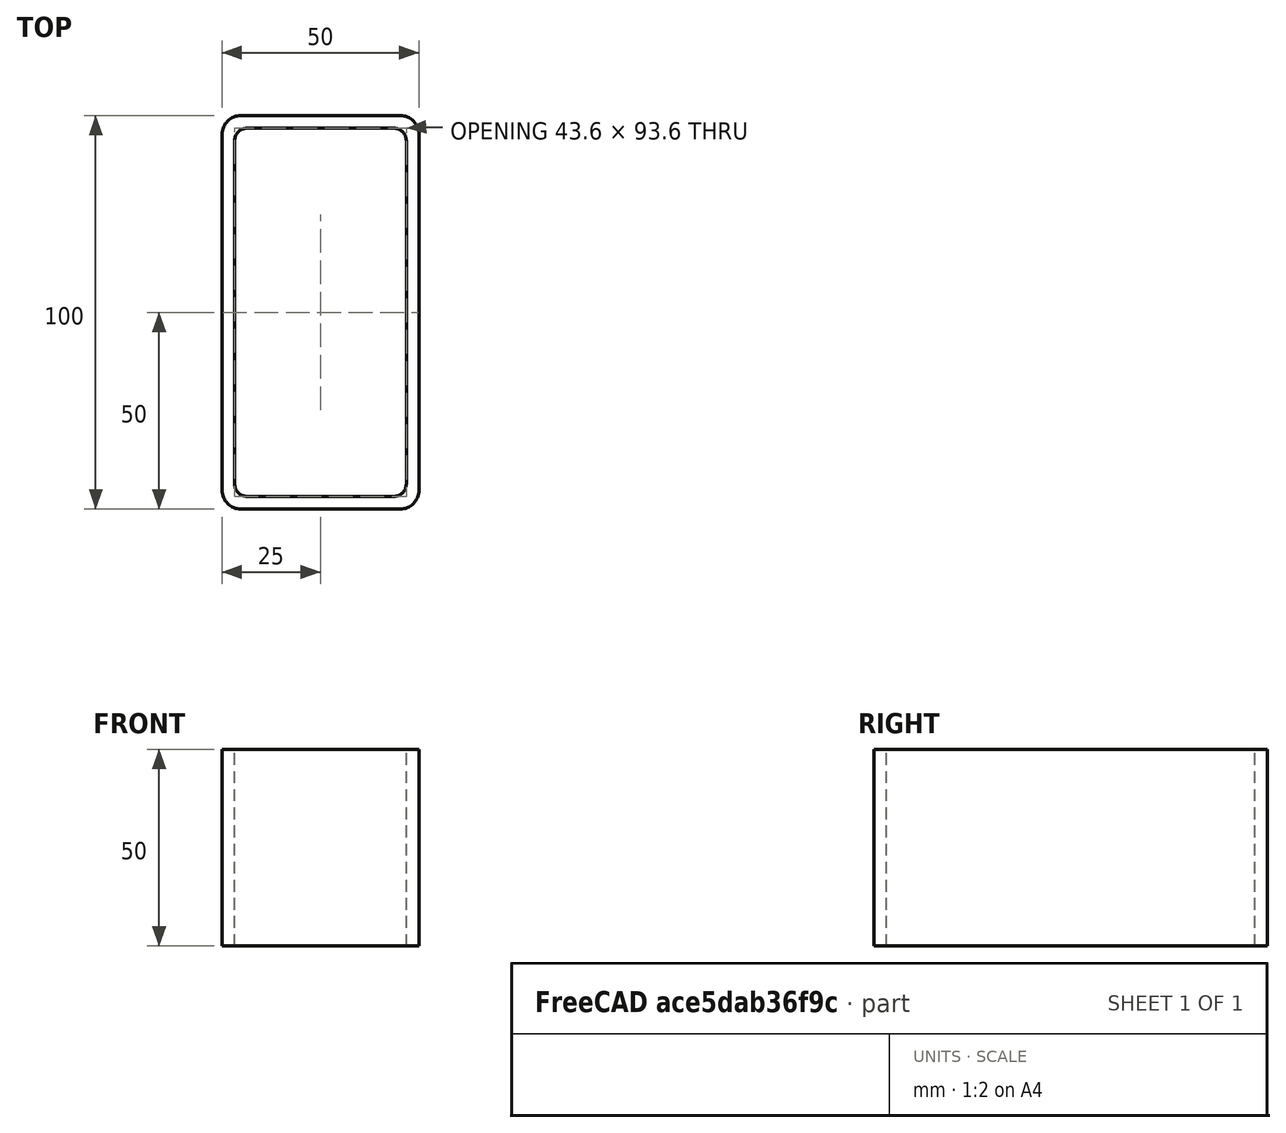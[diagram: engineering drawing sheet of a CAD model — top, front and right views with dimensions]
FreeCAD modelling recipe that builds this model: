
FCSTD DOCUMENT  (FreeCAD 0.15R4671 (Git))
Label: Rectangular hollow section 100x50x3.2 EN10219 S235JRH
License: All rights reserved
LicenseURL: http://en.wikipedia.org/wiki/All_rights_reserved
objects: Sketcher::SketchObject×1, Part::Extrusion×1
note: 2 computed .brp shape members not serialized (recipe doc carries the construction recipe); baked Part::Feature solids carry a one-line shape summary decoded from their .brp

FEATURE [Sketcher::SketchObject] Sketch
  sketch-geometry (16):
    g0: LineSegment StartX=-18.6 StartY=46.8 StartZ=0 EndX=18.6 EndY=46.8 EndZ=0
    g1: LineSegment StartX=21.8 StartY=43.6 StartZ=0 EndX=21.8 EndY=-43.6 EndZ=0
    g2: LineSegment StartX=18.6 StartY=-46.8 StartZ=0 EndX=-18.6 EndY=-46.8 EndZ=0
    g3: LineSegment StartX=-21.8 StartY=-43.6 StartZ=0 EndX=-21.8 EndY=43.6 EndZ=0
    g4: LineSegment StartX=-20.2 StartY=50 StartZ=0 EndX=20.2 EndY=50 EndZ=0
    g5: LineSegment StartX=25 StartY=45.2 StartZ=0 EndX=25 EndY=-45.2 EndZ=0
    g6: LineSegment StartX=20.2 StartY=-50 StartZ=0 EndX=-20.2 EndY=-50 EndZ=0
    g7: LineSegment StartX=-25 StartY=-45.2 StartZ=0 EndX=-25 EndY=45.2 EndZ=0
    g8: ArcOfCircle CenterX=-18.6 CenterY=43.6 CenterZ=0 NormalX=0 NormalY=0 NormalZ=1 Radius=3.2 StartAngle=1.5708 EndAngle=3.14159
    g9: ArcOfCircle CenterX=18.6 CenterY=43.6 CenterZ=0 NormalX=0 NormalY=0 NormalZ=1 Radius=3.2 StartAngle=0 EndAngle=1.5708
    g10: ArcOfCircle CenterX=18.6 CenterY=-43.6 CenterZ=0 NormalX=0 NormalY=0 NormalZ=1 Radius=3.2 StartAngle=4.71239 EndAngle=6.28319
    g11: ArcOfCircle CenterX=-18.6 CenterY=-43.6 CenterZ=0 NormalX=0 NormalY=0 NormalZ=1 Radius=3.2 StartAngle=3.14159 EndAngle=4.71239
    g12: ArcOfCircle CenterX=20.2 CenterY=45.2 CenterZ=0 NormalX=0 NormalY=0 NormalZ=1 Radius=4.8 StartAngle=0 EndAngle=1.5708
    g13: ArcOfCircle CenterX=20.2 CenterY=-45.2 CenterZ=0 NormalX=0 NormalY=0 NormalZ=1 Radius=4.8 StartAngle=4.71239 EndAngle=6.28319
    g14: ArcOfCircle CenterX=-20.2 CenterY=-45.2 CenterZ=0 NormalX=0 NormalY=0 NormalZ=1 Radius=4.8 StartAngle=3.14159 EndAngle=4.71239
    g15: ArcOfCircle CenterX=-20.2 CenterY=45.2 CenterZ=0 NormalX=0 NormalY=0 NormalZ=1 Radius=4.8 StartAngle=1.5708 EndAngle=3.14159
  constraints (36):
    c: Horizontal(g2)
    c: Vertical(g3)
    c: Horizontal(g6)
    c: Vertical(g7)
    c: Tangent(g3,g8) = 1.5708
    c: Tangent(g0,g8) = 1.5708
    c: Tangent(g0,g9) = 1.5708
    c: Tangent(g1,g9) = 1.5708
    c: Tangent(g1,g10) = 1.5708
    c: Tangent(g2,g10) = 1.5708
    c: Tangent(g2,g11) = 1.5708
    c: Tangent(g3,g11) = 1.5708
    c: Tangent(g4,g12) = 1.5708
    c: Tangent(g5,g12) = 1.5708
    c: Tangent(g5,g13) = 1.5708
    c: Tangent(g6,g13) = 1.5708
    c: Tangent(g6,g14) = 1.5708
    c: Tangent(g7,g14) = 1.5708
    c: Tangent(g7,g15) = 1.5708
    c: Tangent(g4,g15) = 1.5708
    c: Equal(g9,g8)
    c: Equal(g9,g11)
    c: Equal(g9,g10)
    c: Equal(g12,g15)
    c: Equal(g12,g14)
    c: Equal(g12,g13)
    c: Symmetric(g4,g6,g-1)
    c: Symmetric(g7,g5,g-2)
    c: DistanceY(g4,g6) = -100
    c: DistanceX(g7,g5) = 50
    c: Symmetric(g3,g1,g-2)
    c: Symmetric(g0,g2,g-1)
    c: DistanceY(g0,g4) = 3.2
    c: DistanceX(g5,g1) = -3.2
    c: Radius(g9) = 3.2
    c: Radius(g12) = 4.8
FEATURE [Part::Extrusion] Extrude  label="Rectangular hollow section 100x50x3.2 EN10219 S235JRH"
  Base = -> Sketch
  Dir = (0,0,50)
  Solid = true
